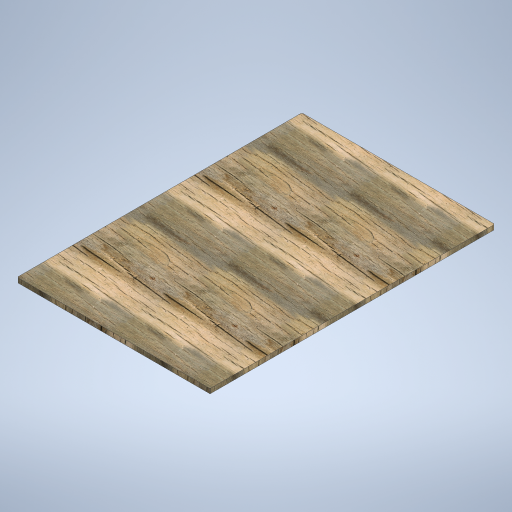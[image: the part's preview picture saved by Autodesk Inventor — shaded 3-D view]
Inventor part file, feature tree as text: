
AUTODESK INVENTOR PART (.ipt)
format: ipt  version: 2023.1 (Build 271208000, 208)  size: 435,712 bytes
history: native  units: in
note: dims shown in document units (in); Inventor stores cm internally (conversion verified against a paired STEP export)
features: extrude x3, sketch x3, chamfer x1
ambient origin geometry x8: Origin, YZ Plane, XZ Plane, XY Plane, X Axis, Y Axis, Z Axis, Center Point
bodies: Solid1 (feature_tree)
feature tree (7):
  extrude  "Extrusion1"  Depth=8.2677in
  chamfer  "Chamfer1"  Distance=0.1969in
  extrude  "Extrusion2"  Depth=11.811in
  extrude  "Extrusion3"  Depth=0.1969in
  sketch  "Sketch1"  dims[d0=12.2047in d1=8.2677in d2=0.1969in d3=0.0in]
  sketch  "Sketch2"  dims[d4=0.0394in d5=0.0787in d6=45.0deg d7=11.811in]
  sketch  "Sketch3"  dims[d8=7.874in d9=0.1969in d10=0.1969in d11=0.1969in d12=0.0in d13=11.0236in d14=7.0866in d15=0.3937in d16=0.3937in d17=0.1969in d18=0.0in]
